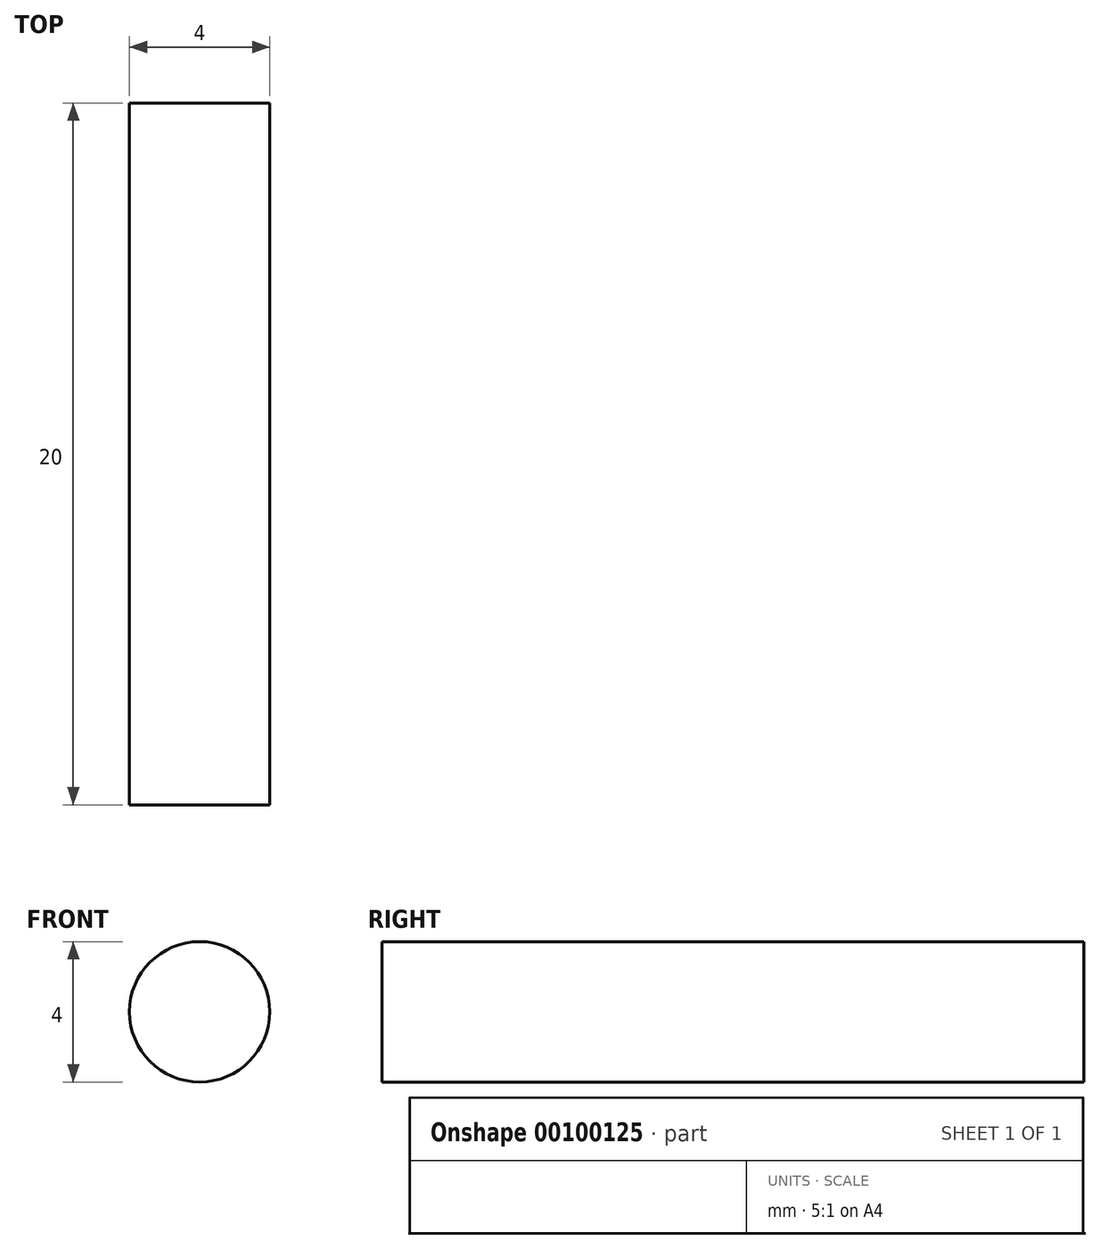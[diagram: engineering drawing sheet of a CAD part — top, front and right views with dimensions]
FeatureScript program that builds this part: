
annotation { "Feature Type Name" : "Feature", "Feature Type Description" : "" }
export const myFeature = defineFeature(function(context is Context, id is Id, definition is map)
    precondition{}
    {
        {
            var Q0;
            Q0=qCreatedBy(makeId("Front.planeOp"),FACE);
            var sketch = newSketch(context, id + "F0", { "sketchPlane" : qUnion([Q0])});
            skCircle(sketch, "E0", {"center": v(0, 0) * mm, "radius": 2 * mm});
            skSolve(sketch);
        }
        {
            var Q0;
            Q0=makeQuery(id+"F0.imprint","IMPRINT",FACE,{"disambiguationData":[TD([[makeQuery(id+"F0.imprint","IMPRINT",EDGE,{"derivedFrom":sQuery(id+"F0.wireOp",EDGE,"E0")}),1.0]])]});
            extrude(context, id + "F1", {"entities" : qUnion([Q0]), "depth" : 20 * mm});
        }
    });
